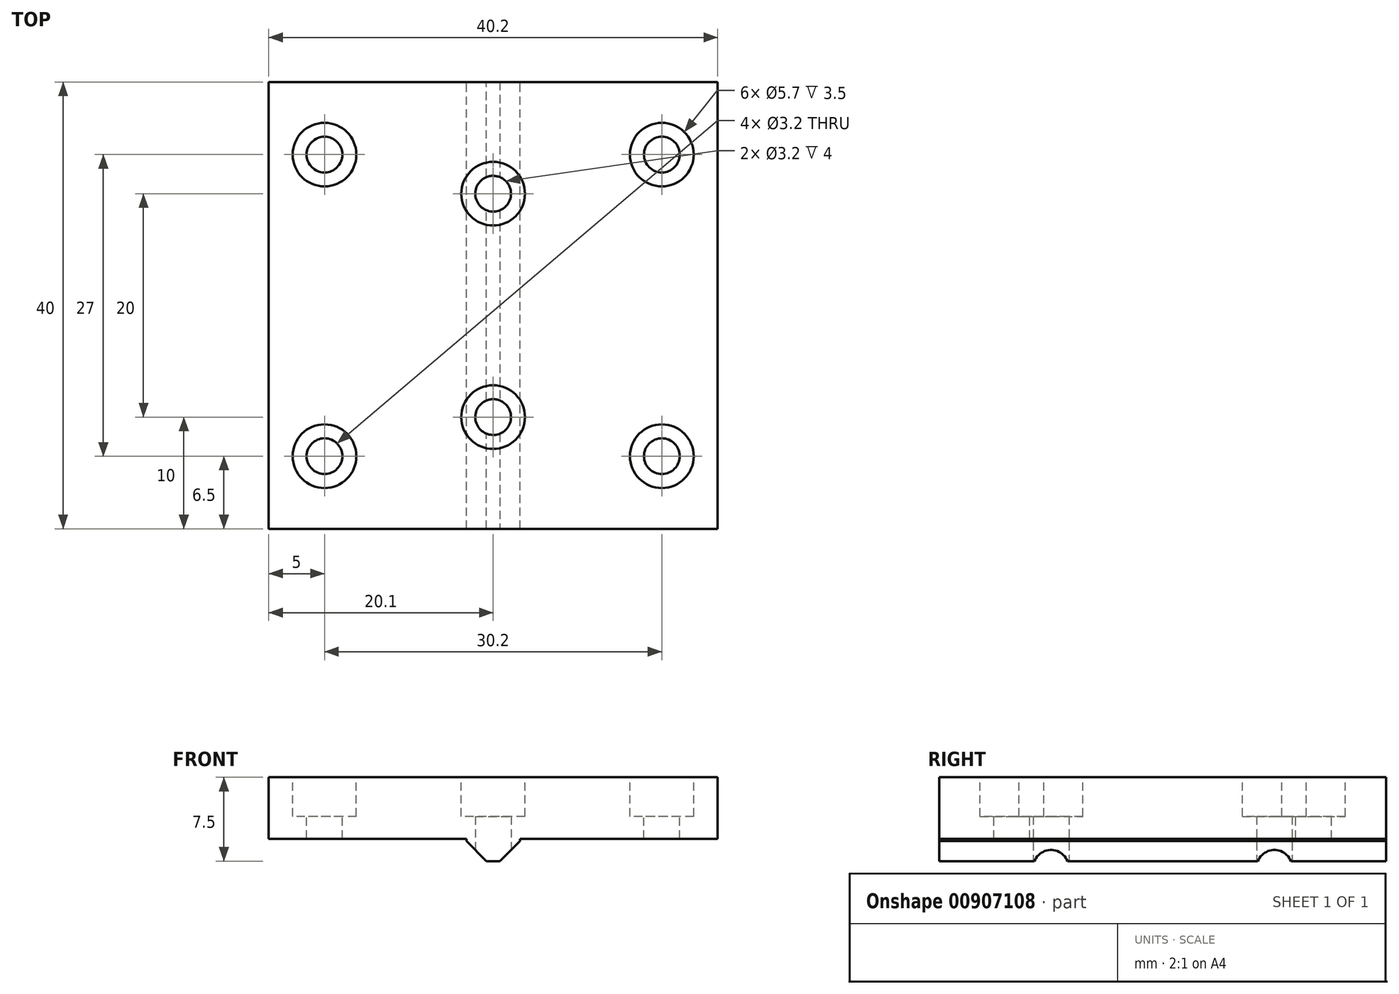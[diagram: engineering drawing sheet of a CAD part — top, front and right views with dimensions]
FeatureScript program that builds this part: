
annotation { "Feature Type Name" : "Feature", "Feature Type Description" : "" }
export const myFeature = defineFeature(function(context is Context, id is Id, definition is map)
    precondition{}
    {
        {
            var Q0;
            Q0=qCreatedBy(makeId("Top.planeOp"),FACE);
            var sketch = newSketch(context, id + "F0", { "sketchPlane" : qUnion([Q0])});
            skLineSegment(sketch, "E0.bottom", {"start": v(0, 0) * mm, "end": v(40.2, 0) * mm});
            skLineSegment(sketch, "E0.top", {"start": v(0, 40) * mm, "end": v(40.2, 40) * mm});
            skLineSegment(sketch, "E0.left", {"start": v(0, 0) * mm, "end": v(0, 40) * mm});
            skLineSegment(sketch, "E0.right", {"start": v(40.2, 0) * mm, "end": v(40.2, 40) * mm});
            skSolve(sketch);
        }
        {
            var Q0;
            Q0 = qSketchRegion(id + "F0", true);
            extrude(context, id + "F1", {"entities" : qUnion([Q0]), "depth" : 5.5 * mm, "offsetDistance" : 25 * mm});
        }
        {
            var Q0;
            Q0=makeQuery(id+"F1.opExtrude","CAP_FACE",FACE,{"disambiguationData":[OSD([sQuery(id+"F0.wireOp",EDGE,"E0.bottom"),sQuery(id+"F0.wireOp",EDGE,"E0.top"),sQuery(id+"F0.wireOp",EDGE,"E0.left"),sQuery(id+"F0.wireOp",EDGE,"E0.right")])],"isStart":false});
            var sketch = newSketch(context, id + "F2", { "sketchPlane" : qUnion([Q0])});
            skLineSegment(sketch, "E1", {"start": v(0, 20) * mm, "end": v(40.2, 20) * mm, "construction": true});
            skLineSegment(sketch, "E2", {"start": v(35.2, 40) * mm, "end": v(35.2, 0) * mm, "construction": true});
            skLineSegment(sketch, "E3", {"start": v(0, 6.5) * mm, "end": v(40.2, 6.5) * mm, "construction": true});
            skLineSegment(sketch, "E4", {"start": v(40.2, 33.5) * mm, "end": v(0, 33.5) * mm, "construction": true});
            skCircle(sketch, "E5", {"center": v(35.2, 6.5) * mm, "radius": 2.85 * mm});
            skCircle(sketch, "E6", {"center": v(35.2, 33.5) * mm, "radius": 2.85 * mm});
            skLineSegment(sketch, "E7", {"start": v(20.1, 40) * mm, "end": v(20.1, 0) * mm, "construction": true});
            skCircle(sketch, "E8.MirrorC", {"center": v(5, 33.5) * mm, "radius": 2.85 * mm});
            skCircle(sketch, "E9.MirrorC", {"center": v(5, 6.5) * mm, "radius": 2.85 * mm});
            skSolve(sketch);
        }
        {
            var Q0;
            Q0 = qSketchRegion(id + "F2", true);
            extrude(context, id + "F3", {"entities" : qUnion([Q0]), "operationType" : NewBodyOperationType.REMOVE, "oppositeDirection" : true, "depth" : 3.5 * mm, "offsetDistance" : 25 * mm});
        }
        {
            var Q0;
            Q0=makeQuery(id+"F2.imprint","IMPRINT",FACE,{"disambiguationData":[TD([[makeQuery(id+"F2.imprint","IMPRINT",EDGE,{"derivedFrom":sQuery(id+"F2.wireOp",EDGE,"E5")}),-1.0]])]});
            var sketch = newSketch(context, id + "F4", { "sketchPlane" : qUnion([Q0])});
            skCircle(sketch, "E10", {"center": v(35.2, 33.5) * mm, "radius": 1.6 * mm});
            skCircle(sketch, "E11", {"center": v(35.2, 6.5) * mm, "radius": 1.6 * mm});
            skCircle(sketch, "E12.MirrorC", {"center": v(5, 33.5) * mm, "radius": 1.6 * mm});
            skCircle(sketch, "E13.MirrorC", {"center": v(5, 6.5) * mm, "radius": 1.6 * mm});
            skSolve(sketch);
        }
        {
            var Q0;
            Q0 = qSketchRegion(id + "F4", true);
            extrude(context, id + "F5", {"entities" : qUnion([Q0]), "operationType" : NewBodyOperationType.REMOVE, "oppositeDirection" : true, "depth" : 25 * mm, "offsetDistance" : 25 * mm});
        }
        {
            var Q0;
            Q0=makeQuery(id+"F1.opExtrude","CAP_FACE",FACE,{"disambiguationData":[OSD([sQuery(id+"F0.wireOp",EDGE,"E0.bottom"),sQuery(id+"F0.wireOp",EDGE,"E0.top"),sQuery(id+"F0.wireOp",EDGE,"E0.left"),sQuery(id+"F0.wireOp",EDGE,"E0.right")])],"isStart":true});
            var sketch = newSketch(context, id + "F6", { "sketchPlane" : qUnion([Q0])});
            skLineSegment(sketch, "E14.bottom", {"start": v(17.7, 0) * mm, "end": v(22.5, 0) * mm});
            skLineSegment(sketch, "E14.top", {"start": v(17.7, -40) * mm, "end": v(22.5, -40) * mm});
            skLineSegment(sketch, "E14.left", {"start": v(22.5, 0) * mm, "end": v(22.5, -40) * mm});
            skLineSegment(sketch, "E14.right", {"start": v(17.7, 0) * mm, "end": v(17.7, -40) * mm});
            skSolve(sketch);
        }
        {
            var Q0;
            Q0 = qSketchRegion(id + "F6", true);
            extrude(context, id + "F7", {"entities" : qUnion([Q0]), "operationType" : NewBodyOperationType.ADD, "depth" : 2 * mm, "offsetDistance" : 25 * mm});
        }
        {
            var Q0;
            Q0=makeQuery(id+"F7.opExtrude","CAP_EDGE",EDGE,{"disambiguationData":[OSD([sQuery(id+"F6.wireOp",EDGE,"E14.right")])],"isStart":false});
            var Q1;
            Q1=makeQuery(id+"F7.opExtrude","CAP_EDGE",EDGE,{"disambiguationData":[OSD([sQuery(id+"F6.wireOp",EDGE,"E14.left")])],"isStart":false});
            chamfer(context, id + "F8", {"entities" : qUnion([Q0, Q1]), "width" : 1.8 * mm, "tangentPropagation" : true});
        }
        {
            var Q0;
            Q0=makeQuery(id+"F7.opExtrude","CAP_FACE",FACE,{"disambiguationData":[OSD([sQuery(id+"F6.wireOp",EDGE,"E14.bottom"),sQuery(id+"F6.wireOp",EDGE,"E14.top"),sQuery(id+"F6.wireOp",EDGE,"E14.left"),sQuery(id+"F6.wireOp",EDGE,"E14.right")])],"isStart":false});
            var sketch = newSketch(context, id + "F9", { "sketchPlane" : qUnion([Q0])});
            skCircle(sketch, "E15", {"center": v(20.1, -30) * mm, "radius": 1.6 * mm});
            skLineSegment(sketch, "E16", {"start": v(20.1, 0) * mm, "end": v(20.1, -40) * mm, "construction": true});
            skLineSegment(sketch, "E17", {"start": v(20.7, -30) * mm, "end": v(19.5, -30) * mm, "construction": true});
            skLineSegment(sketch, "E18", {"start": v(20.7, -10) * mm, "end": v(19.5, -10) * mm, "construction": true});
            skPoint(sketch, "E19", {"position": v(20.1, -10) * mm});
            skCircle(sketch, "E20", {"center": v(20.1, -10) * mm, "radius": 1.6 * mm});
            skSolve(sketch);
        }
        {
            var Q0;
            Q0 = qSketchRegion(id + "F9", true);
            extrude(context, id + "F10", {"entities" : qUnion([Q0]), "operationType" : NewBodyOperationType.REMOVE, "oppositeDirection" : true, "depth" : 25 * mm, "offsetDistance" : 25 * mm});
        }
        {
            var Q0;
            Q0=makeQuery(id+"F2.imprint","IMPRINT",FACE,{"disambiguationData":[TD([[makeQuery(id+"F2.imprint","IMPRINT",EDGE,{"derivedFrom":sQuery(id+"F2.wireOp",EDGE,"E5")}),-1.0]])]});
            var sketch = newSketch(context, id + "F11", { "sketchPlane" : qUnion([Q0])});
            skCircle(sketch, "E21", {"center": v(20.1, 30) * mm, "radius": 2.85 * mm});
            skCircle(sketch, "E22.MirrorC", {"center": v(20.1, 10) * mm, "radius": 2.85 * mm});
            skSolve(sketch);
        }
        {
            var Q0;
            Q0 = qSketchRegion(id + "F11", true);
            extrude(context, id + "F12", {"entities" : qUnion([Q0]), "operationType" : NewBodyOperationType.REMOVE, "oppositeDirection" : true, "depth" : 3.5 * mm, "offsetDistance" : 25 * mm});
        }
    });
